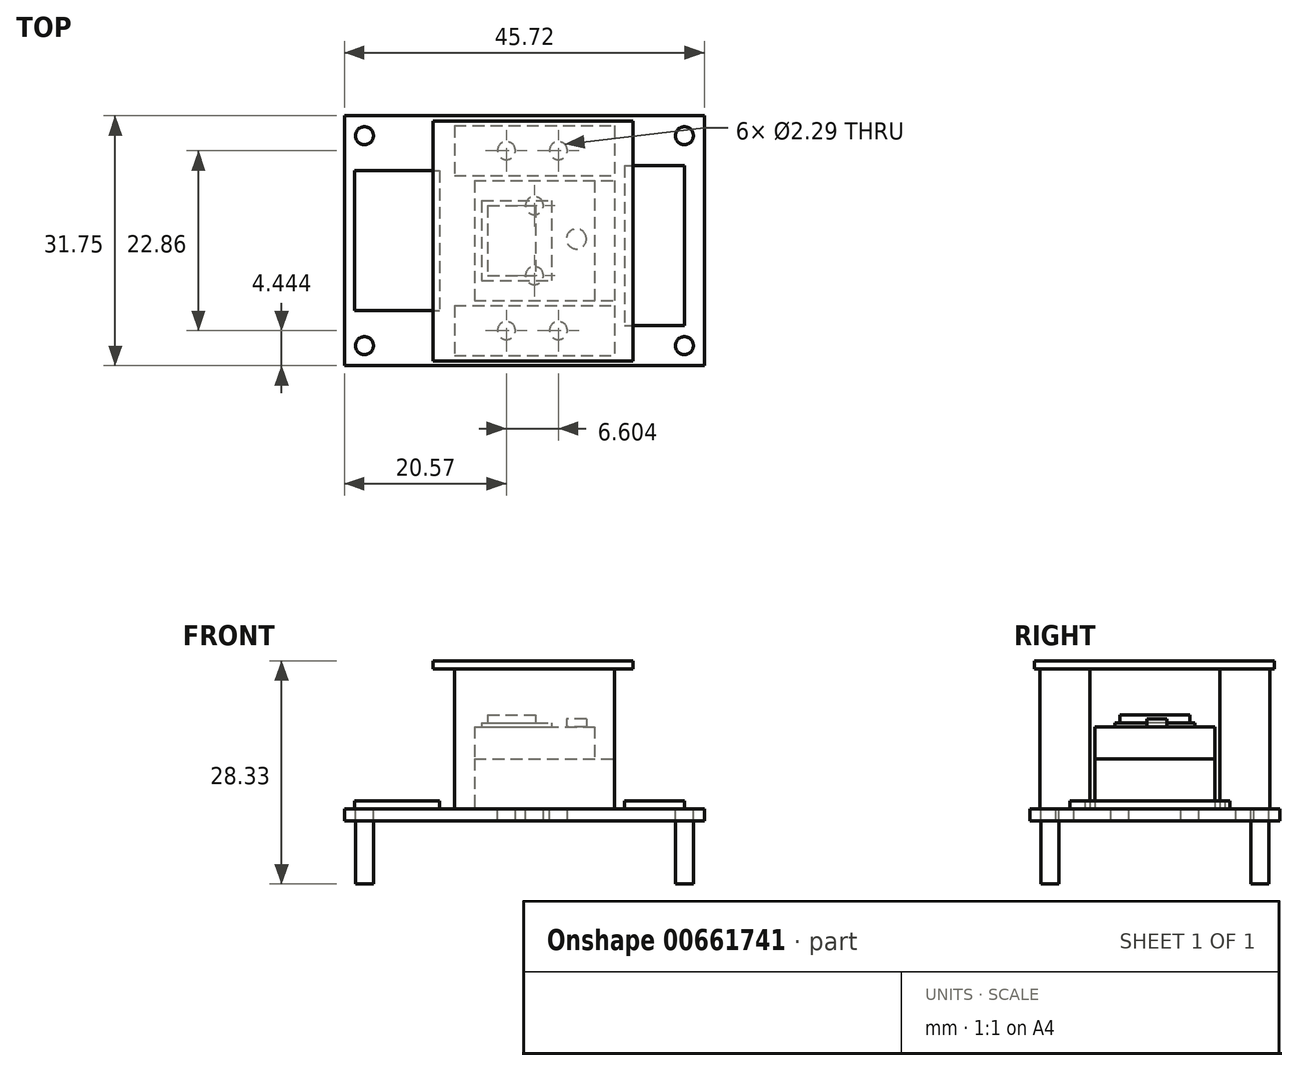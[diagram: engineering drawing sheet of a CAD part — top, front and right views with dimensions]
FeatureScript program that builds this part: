
annotation { "Feature Type Name" : "Feature", "Feature Type Description" : "" }
export const myFeature = defineFeature(function(context is Context, id is Id, definition is map)
    precondition{}
    {
        {
            var Q0;
            Q0=qCreatedBy(makeId("Top.planeOp"),FACE);
            var sketch = newSketch(context, id + "F0", { "sketchPlane" : qUnion([Q0])});
            skLineSegment(sketch, "E0.bottom", {"start": v(-22.76, 15.9) * mm, "end": v(22.96, 15.9) * mm});
            skLineSegment(sketch, "E0.top", {"start": v(-22.76, -15.85) * mm, "end": v(22.96, -15.85) * mm});
            skLineSegment(sketch, "E0.left", {"start": v(-22.76, 15.9) * mm, "end": v(-22.76, -15.85) * mm});
            skLineSegment(sketch, "E0.right", {"start": v(22.96, 15.9) * mm, "end": v(22.96, -15.85) * mm});
            skCircle(sketch, "E1", {"center": v(1.37, 4.47) * mm, "radius": 1.14 * mm});
            skCircle(sketch, "E2", {"center": v(1.37, -4.42) * mm, "radius": 1.14 * mm});
            skCircle(sketch, "E3", {"center": v(-2.2, -11.4) * mm, "radius": 1.14 * mm});
            skCircle(sketch, "E4", {"center": v(-2.2, 11.45) * mm, "radius": 1.14 * mm});
            skCircle(sketch, "E5", {"center": v(4.41, 11.45) * mm, "radius": 1.14 * mm});
            skCircle(sketch, "E6", {"center": v(4.41, -11.4) * mm, "radius": 1.14 * mm});
            skSolve(sketch);
        }
        {
            var Q0;
            Q0=makeQuery(id+"F0.imprint","IMPRINT",FACE,{"disambiguationData":[TD([[makeQuery(id+"F0.imprint","IMPRINT",EDGE,{"derivedFrom":sQuery(id+"F0.wireOp",EDGE,"E0.bottom")}),-1.0]])]});
            extrude(context, id + "F1", {"entities" : qUnion([Q0]), "oppositeDirection" : true, "depth" : 1.52 * mm, "offsetDistance" : 25.4 * mm});
        }
        {
            var Q0;
            Q0=qCreatedBy(makeId("Top.planeOp"),FACE);
            var sketch = newSketch(context, id + "F2", { "sketchPlane" : qUnion([Q0])});
            skCircle(sketch, "E7", {"center": v(-20.22, 13.36) * mm, "radius": 1.14 * mm});
            skCircle(sketch, "E8", {"center": v(-20.22, -13.31) * mm, "radius": 1.14 * mm});
            skCircle(sketch, "E9", {"center": v(20.42, -13.31) * mm, "radius": 1.14 * mm});
            skCircle(sketch, "E10", {"center": v(20.42, 13.36) * mm, "radius": 1.14 * mm});
            skSolve(sketch);
        }
        {
            var Q0;
            Q0 = qSketchRegion(id + "F2", true);
            extrude(context, id + "F3", {"entities" : qUnion([Q0]), "oppositeDirection" : true, "depth" : 9.52 * mm, "offsetDistance" : 25.4 * mm});
        }
        {
            var Q0;
            Q0=qCreatedBy(makeId("Top.planeOp"),FACE);
            var sketch = newSketch(context, id + "F4", { "sketchPlane" : qUnion([Q0])});
            skLineSegment(sketch, "E11.bottom", {"start": v(-6.25, 7.64) * mm, "end": v(11.53, 7.64) * mm});
            skLineSegment(sketch, "E11.top", {"start": v(-6.25, -7.6) * mm, "end": v(11.53, -7.6) * mm});
            skLineSegment(sketch, "E11.left", {"start": v(-6.25, 7.64) * mm, "end": v(-6.25, -7.6) * mm});
            skLineSegment(sketch, "E11.right", {"start": v(11.53, 7.64) * mm, "end": v(11.53, -7.6) * mm});
            skSolve(sketch);
        }
        {
            var Q0;
            Q0 = qSketchRegion(id + "F4", true);
            extrude(context, id + "F5", {"entities" : qUnion([Q0]), "depth" : 6.35 * mm, "offsetDistance" : 25.4 * mm});
        }
        {
            var Q0;
            Q0=makeQuery(id+"F5.opExtrude","CAP_FACE",FACE,{"disambiguationData":[OSD([sQuery(id+"F4.wireOp",EDGE,"E11.bottom"),sQuery(id+"F4.wireOp",EDGE,"E11.top"),sQuery(id+"F4.wireOp",EDGE,"E11.left"),sQuery(id+"F4.wireOp",EDGE,"E11.right")])],"isStart":false});
            var sketch = newSketch(context, id + "F6", { "sketchPlane" : qUnion([Q0])});
            skLineSegment(sketch, "E12.bottom", {"start": v(-6.25, 7.64) * mm, "end": v(8.99, 7.64) * mm});
            skLineSegment(sketch, "E12.top", {"start": v(-6.25, -7.6) * mm, "end": v(8.99, -7.6) * mm});
            skLineSegment(sketch, "E12.left", {"start": v(-6.25, 7.64) * mm, "end": v(-6.25, -7.6) * mm});
            skLineSegment(sketch, "E12.right", {"start": v(8.99, 7.64) * mm, "end": v(8.99, -7.6) * mm});
            skSolve(sketch);
        }
        {
            var Q0;
            Q0 = qSketchRegion(id + "F6", true);
            extrude(context, id + "F7", {"entities" : qUnion([Q0]), "depth" : 4.06 * mm, "offsetDistance" : 25.4 * mm});
        }
        {
            var Q0;
            Q0=makeQuery(id+"F0.imprint","IMPRINT",FACE,{"disambiguationData":[TD([[makeQuery(id+"F0.imprint","IMPRINT",EDGE,{"derivedFrom":sQuery(id+"F0.wireOp",EDGE,"E0.bottom")}),-1.0]])]});
            var sketch = newSketch(context, id + "F8", { "sketchPlane" : qUnion([Q0])});
            skLineSegment(sketch, "E13.bottom", {"start": v(-8.8, -8.23) * mm, "end": v(11.53, -8.23) * mm});
            skLineSegment(sketch, "E13.top", {"start": v(-8.8, -14.58) * mm, "end": v(11.53, -14.58) * mm});
            skLineSegment(sketch, "E13.left", {"start": v(-8.8, -8.23) * mm, "end": v(-8.8, -14.58) * mm});
            skLineSegment(sketch, "E13.right", {"start": v(11.53, -8.23) * mm, "end": v(11.53, -14.58) * mm});
            skLineSegment(sketch, "E14.bottom", {"start": v(-8.8, 14.63) * mm, "end": v(11.53, 14.63) * mm});
            skLineSegment(sketch, "E14.top", {"start": v(-8.8, 8.28) * mm, "end": v(11.53, 8.28) * mm});
            skLineSegment(sketch, "E14.left", {"start": v(-8.8, 14.63) * mm, "end": v(-8.8, 8.28) * mm});
            skLineSegment(sketch, "E14.right", {"start": v(11.53, 14.63) * mm, "end": v(11.53, 8.28) * mm});
            skSolve(sketch);
        }
        {
            var Q0;
            Q0 = qSketchRegion(id + "F8", true);
            extrude(context, id + "F9", {"entities" : qUnion([Q0]), "depth" : 17.78 * mm, "offsetDistance" : 25.4 * mm});
        }
        {
            var Q0;
            Q0=makeQuery(id+"F7.opExtrude","CAP_FACE",FACE,{"disambiguationData":[OSD([sQuery(id+"F6.wireOp",EDGE,"E12.bottom"),sQuery(id+"F6.wireOp",EDGE,"E12.top"),sQuery(id+"F6.wireOp",EDGE,"E12.left"),sQuery(id+"F6.wireOp",EDGE,"E12.right")])],"isStart":false});
            var sketch = newSketch(context, id + "F10", { "sketchPlane" : qUnion([Q0])});
            skLineSegment(sketch, "E15.bottom", {"start": v(-5.33, 5.1) * mm, "end": v(3.56, 5.1) * mm});
            skLineSegment(sketch, "E15.top", {"start": v(-5.33, -5.06) * mm, "end": v(3.56, -5.06) * mm});
            skLineSegment(sketch, "E15.left", {"start": v(-5.33, 5.1) * mm, "end": v(-5.33, -5.06) * mm});
            skLineSegment(sketch, "E15.right", {"start": v(3.56, 5.1) * mm, "end": v(3.56, -5.06) * mm});
            skSolve(sketch);
        }
        {
            var Q0;
            Q0 = qSketchRegion(id + "F10", true);
            extrude(context, id + "F11", {"entities" : qUnion([Q0]), "depth" : 0.5 * mm, "offsetDistance" : 25.4 * mm});
        }
        {
            var Q0;
            Q0=makeQuery(id+"F11.opExtrude","CAP_FACE",FACE,{"disambiguationData":[OSD([sQuery(id+"F10.wireOp",EDGE,"E15.bottom"),sQuery(id+"F10.wireOp",EDGE,"E15.top"),sQuery(id+"F10.wireOp",EDGE,"E15.left"),sQuery(id+"F10.wireOp",EDGE,"E15.right")])],"isStart":false});
            var sketch = newSketch(context, id + "F12", { "sketchPlane" : qUnion([Q0])});
            skLineSegment(sketch, "E16.bottom", {"start": v(-4.59, 4.47) * mm, "end": v(1.5, 4.47) * mm});
            skLineSegment(sketch, "E16.top", {"start": v(-4.59, -4.42) * mm, "end": v(1.5, -4.42) * mm});
            skLineSegment(sketch, "E16.left", {"start": v(-4.59, 4.47) * mm, "end": v(-4.59, -4.42) * mm});
            skLineSegment(sketch, "E16.right", {"start": v(1.5, 4.47) * mm, "end": v(1.5, -4.42) * mm});
            skSolve(sketch);
        }
        {
            var Q0;
            Q0 = qSketchRegion(id + "F12", true);
            extrude(context, id + "F13", {"entities" : qUnion([Q0]), "depth" : 1.02 * mm, "offsetDistance" : 25.4 * mm});
        }
        {
            var Q0;
            Q0=makeQuery(id+"F10.imprint","IMPRINT",FACE,{"disambiguationData":[TD([[makeQuery(id+"F10.imprint","IMPRINT",EDGE,{"derivedFrom":sQuery(id+"F10.wireOp",EDGE,"E15.bottom")}),1.0]])]});
            var sketch = newSketch(context, id + "F14", { "sketchPlane" : qUnion([Q0])});
            skCircle(sketch, "E17", {"center": v(6.7, 0.24) * mm, "radius": 1.27 * mm});
            skSolve(sketch);
        }
        {
            var Q0;
            Q0 = qSketchRegion(id + "F14", true);
            extrude(context, id + "F15", {"entities" : qUnion([Q0]), "depth" : 1.02 * mm, "offsetDistance" : 25.4 * mm});
        }
        {
            var Q0;
            Q0=makeQuery(id+"F9.opExtrude","CAP_FACE",FACE,{"disambiguationData":[OSD([sQuery(id+"F8.wireOp",EDGE,"E14.bottom"),sQuery(id+"F8.wireOp",EDGE,"E14.top"),sQuery(id+"F8.wireOp",EDGE,"E14.left"),sQuery(id+"F8.wireOp",EDGE,"E14.right")])],"isStart":false});
            var sketch = newSketch(context, id + "F16", { "sketchPlane" : qUnion([Q0])});
            skLineSegment(sketch, "E18.bottom", {"start": v(-11.53, 15.2) * mm, "end": v(13.87, 15.2) * mm});
            skLineSegment(sketch, "E18.top", {"start": v(-11.53, -15.28) * mm, "end": v(13.87, -15.28) * mm});
            skLineSegment(sketch, "E18.left", {"start": v(-11.53, 15.2) * mm, "end": v(-11.53, -15.28) * mm});
            skLineSegment(sketch, "E18.right", {"start": v(13.87, 15.2) * mm, "end": v(13.87, -15.28) * mm});
            skSolve(sketch);
        }
        {
            var Q0;
            Q0 = qSketchRegion(id + "F16", true);
            extrude(context, id + "F17", {"entities" : qUnion([Q0]), "depth" : 1.02 * mm, "offsetDistance" : 25.4 * mm});
        }
        {
            var Q0;
            Q0=makeQuery(id+"F0.imprint","IMPRINT",FACE,{"disambiguationData":[TD([[makeQuery(id+"F0.imprint","IMPRINT",EDGE,{"derivedFrom":sQuery(id+"F0.wireOp",EDGE,"E0.bottom")}),-1.0]])]});
            var sketch = newSketch(context, id + "F18", { "sketchPlane" : qUnion([Q0])});
            skLineSegment(sketch, "E19.bottom", {"start": v(-21.5, 8.91) * mm, "end": v(-10.7, 8.91) * mm});
            skLineSegment(sketch, "E19.top", {"start": v(-21.5, -8.87) * mm, "end": v(-10.7, -8.87) * mm});
            skLineSegment(sketch, "E19.left", {"start": v(-21.5, 8.91) * mm, "end": v(-21.5, -8.87) * mm});
            skLineSegment(sketch, "E19.right", {"start": v(-10.7, 8.91) * mm, "end": v(-10.7, -8.87) * mm});
            skLineSegment(sketch, "E20.bottom", {"start": v(12.8, 9.55) * mm, "end": v(20.42, 9.55) * mm});
            skLineSegment(sketch, "E20.top", {"start": v(12.8, -10.77) * mm, "end": v(20.42, -10.77) * mm});
            skLineSegment(sketch, "E20.left", {"start": v(12.8, 9.55) * mm, "end": v(12.8, -10.77) * mm});
            skLineSegment(sketch, "E20.right", {"start": v(20.42, 9.55) * mm, "end": v(20.42, -10.77) * mm});
            skSolve(sketch);
        }
        {
            var Q0;
            Q0 = qSketchRegion(id + "F18", true);
            extrude(context, id + "F19", {"entities" : qUnion([Q0]), "depth" : 1.02 * mm, "offsetDistance" : 25.4 * mm});
        }
    });
